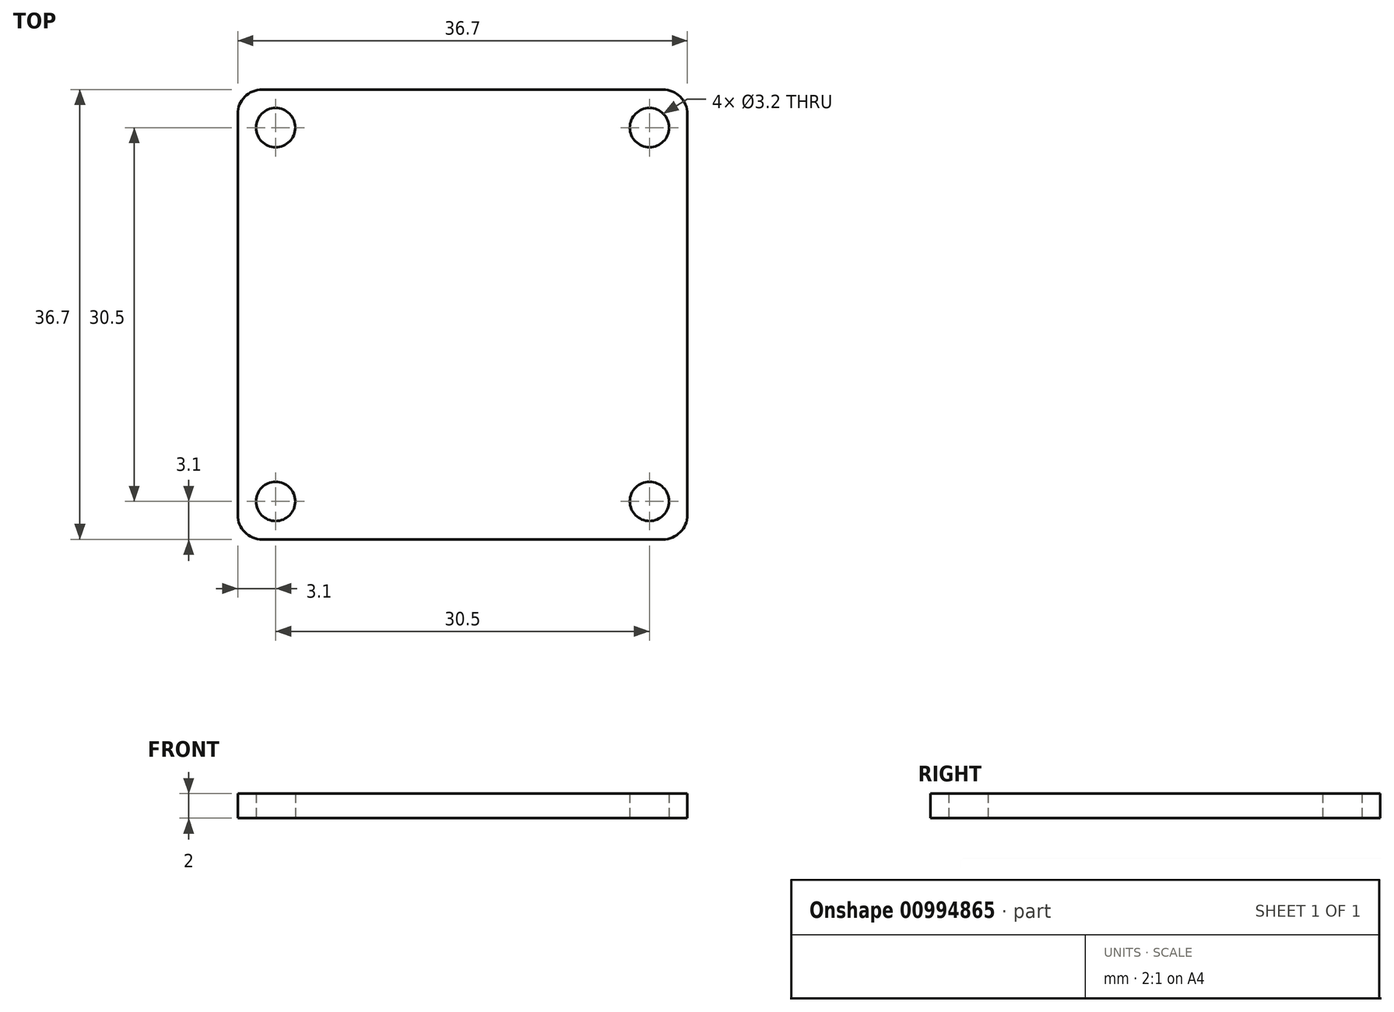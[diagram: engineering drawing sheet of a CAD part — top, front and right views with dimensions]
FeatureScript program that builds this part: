
annotation { "Feature Type Name" : "Feature", "Feature Type Description" : "" }
export const myFeature = defineFeature(function(context is Context, id is Id, definition is map)
    precondition{}
    {
        {
            var Q0;
            Q0=qCreatedBy(makeId("Top.planeOp"),FACE);
            var sketch = newSketch(context, id + "F0", { "sketchPlane" : qUnion([Q0])});
            skPoint(sketch, "E0.middle", {"position": v(0, 0) * mm});
            skCircle(sketch, "E1", {"center": v(15.25, 15.25) * mm, "radius": 1.6 * mm});
            skCircle(sketch, "E2", {"center": v(-15.25, 15.25) * mm, "radius": 1.6 * mm});
            skCircle(sketch, "E3.MirrorC", {"center": v(15.25, -15.25) * mm, "radius": 1.6 * mm});
            skCircle(sketch, "E4.MirrorC", {"center": v(-15.25, -15.25) * mm, "radius": 1.6 * mm});
            skLineSegment(sketch, "E5.bottom", {"start": v(18.35, 18.35) * mm, "end": v(-18.35, 18.35) * mm});
            skLineSegment(sketch, "E5.top", {"start": v(18.35, -18.35) * mm, "end": v(-18.35, -18.35) * mm});
            skLineSegment(sketch, "E5.left", {"start": v(18.35, 18.35) * mm, "end": v(18.35, -18.35) * mm});
            skLineSegment(sketch, "E5.right", {"start": v(-18.35, 18.35) * mm, "end": v(-18.35, -18.35) * mm});
            skSolve(sketch);
        }
        {
            var Q0;
            Q0 = qSketchRegion(id + "F0", true);
            extrude(context, id + "F1", {"entities" : qUnion([Q0]), "depth" : 2 * mm, "offsetDistance" : 25 * mm});
        }
        {
            var Q0;
            Q0=makeQuery(id+"F1.opExtrude","SWEPT_EDGE",EDGE,{"disambiguationData":[OSD([sQuery(id+"F0.wireOp",EDGE,"E5.bottom"),sQuery(id+"F0.wireOp",EDGE,"E5.right")])]});
            var Q1;
            Q1=makeQuery(id+"F1.opExtrude","SWEPT_EDGE",EDGE,{"disambiguationData":[OSD([sQuery(id+"F0.wireOp",EDGE,"E5.bottom"),sQuery(id+"F0.wireOp",EDGE,"E5.left")])]});
            var Q2;
            Q2=makeQuery(id+"F1.opExtrude","SWEPT_EDGE",EDGE,{"disambiguationData":[OSD([sQuery(id+"F0.wireOp",EDGE,"E5.top"),sQuery(id+"F0.wireOp",EDGE,"E5.left")])]});
            var Q3;
            Q3=makeQuery(id+"F1.opExtrude","SWEPT_EDGE",EDGE,{"disambiguationData":[OSD([sQuery(id+"F0.wireOp",EDGE,"E5.top"),sQuery(id+"F0.wireOp",EDGE,"E5.right")])]});
            fillet(context, id + "F2", {"entities" : qUnion([Q0, Q1, Q2, Q3]), "radius" : 2 * mm, "tangentPropagation" : true, "allowEdgeOverflow" : false});
        }
    });
